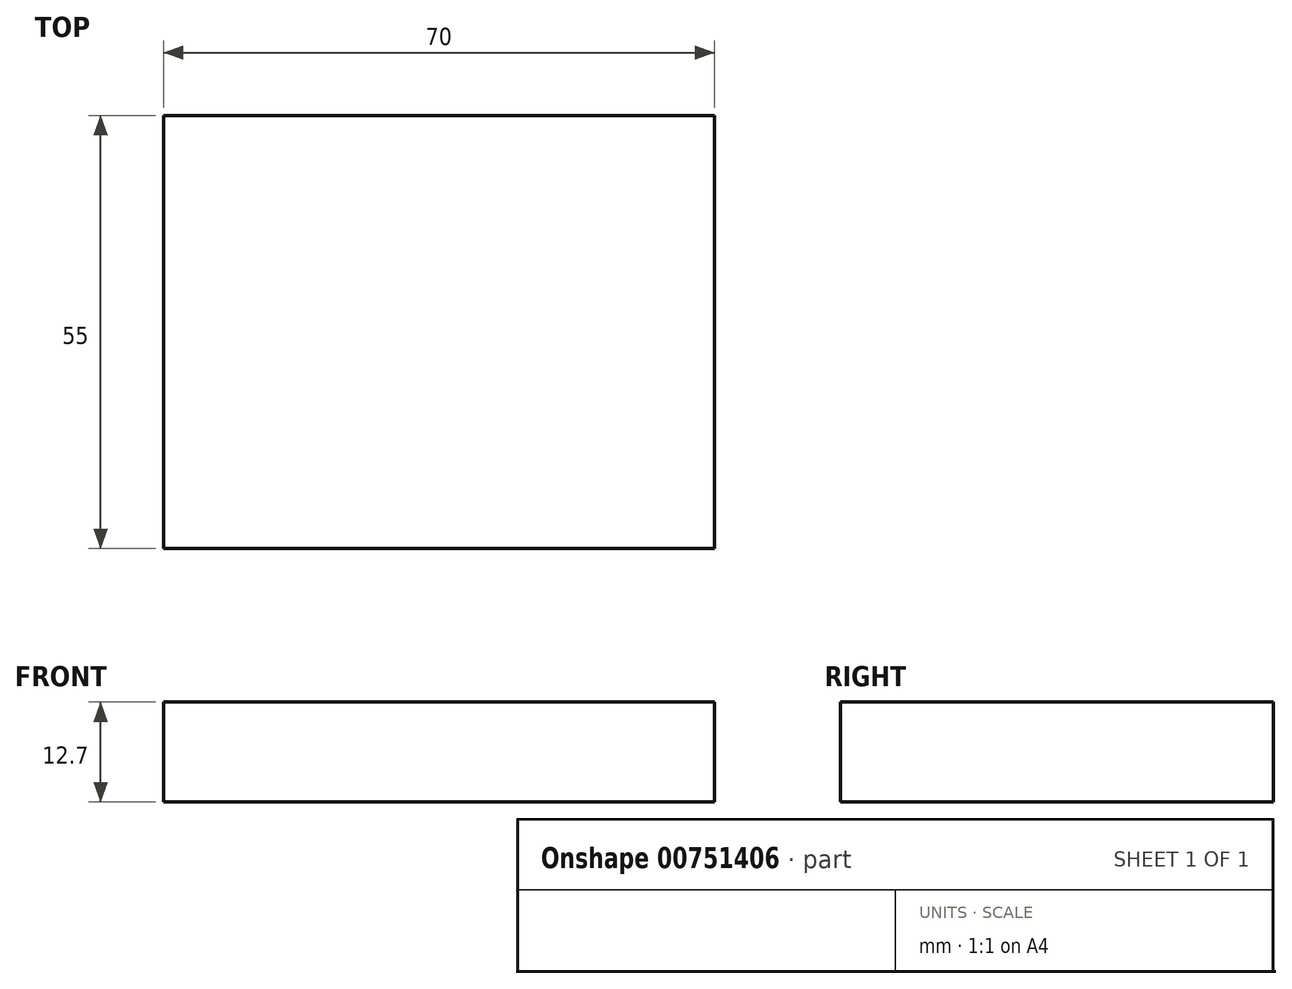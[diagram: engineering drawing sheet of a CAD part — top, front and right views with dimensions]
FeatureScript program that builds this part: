
annotation { "Feature Type Name" : "Feature", "Feature Type Description" : "" }
export const myFeature = defineFeature(function(context is Context, id is Id, definition is map)
    precondition{}
    {
        {
            var Q0;
            Q0=qCreatedBy(makeId("Top.planeOp"),FACE);
            var sketch = newSketch(context, id + "F0", { "sketchPlane" : qUnion([Q0])});
            skLineSegment(sketch, "E0.bottom", {"start": v(-35, 27.5) * mm, "end": v(35, 27.5) * mm});
            skLineSegment(sketch, "E0.top", {"start": v(-35, -27.5) * mm, "end": v(35, -27.5) * mm});
            skLineSegment(sketch, "E0.left", {"start": v(-35, 27.5) * mm, "end": v(-35, -27.5) * mm});
            skLineSegment(sketch, "E0.right", {"start": v(35, 27.5) * mm, "end": v(35, -27.5) * mm});
            skLineSegment(sketch, "E1", {"start": v(-35, 27.5) * mm, "end": v(35, -27.5) * mm, "construction": true});
            skLineSegment(sketch, "E2", {"start": v(35, 27.5) * mm, "end": v(-35, -27.5) * mm, "construction": true});
            skPoint(sketch, "E3", {"position": v(0, 0) * mm});
            skSolve(sketch);
        }
        {
            var Q0;
            Q0=makeQuery(id+"F0.imprint","IMPRINT",FACE,{"disambiguationData":[TD([[makeQuery(id+"F0.imprint","IMPRINT",EDGE,{"derivedFrom":sQuery(id+"F0.wireOp",EDGE,"E0.bottom")}),-1.0]])]});
            extrude(context, id + "F1", {"entities" : qUnion([Q0]), "depth" : 12.7 * mm, "offsetDistance" : 25.4 * mm});
        }
    });
